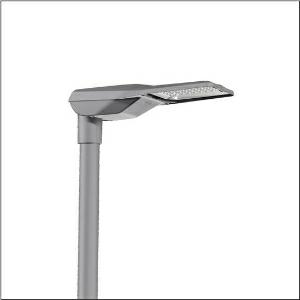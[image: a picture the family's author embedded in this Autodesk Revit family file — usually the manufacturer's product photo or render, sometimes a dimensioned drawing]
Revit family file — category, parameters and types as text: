
# Revit family: streetlight_sl_21_iq_mini___p0_8ab_5xe2r31d08jb_fb45
name_source: partatom
category: Lighting Fixtures
units: mm (PartAtom-declared; Revit-internal decimal feet)

## family parameters
Cut with Voids When Loaded = No
Host = Face
Light Source = No
Part Type = Normal
Room Calculation Point = No
Round Connector Dimension = Use Diameter
Shared = No

## types (1)
- --- (1 x LED, 9400 lm, 71.6 W, 3000K)
    Apparent Load = 72 VA
    CIE Flux Codes = 39 72 97 100 100
    Color Rendering = 70
    Color Temperature = 3000K
    Default Elevation = 1800 mm
    Description = Streetlight SL 21 iQ mini, mast luminaire, primary light control with lens, of PMMA, primary optical cover: cover, of toughened safety glass, transparent, light distribution: P0.8aB, light emission: direct distribution, primary light characteristic: asymmetric, installation type: post-top, side-entry, LED, High Power LED, rated luminous flux: 9.400lm, luminous efficacy: 131lm/W, light colour: 730, colour temperature: 3000K, control gear: iQ-Comfort, control: pre-setting: linear dimming characteristic, Auto-Match, Temp-Guard, Lumen-Switch, Night-Set, Smart-Wire, Light-Fading, Desk-Remote (wireless, voltage-free reading and setting of iQ features in the workshop via application-optimized NFC function/RFID function), optimised constant luminous flux control (CLO 2.0), mains connection: 220..240V, AC, 50/60Hz, start of lifetime: 72W, end of service life: 75W, reduction: 33W, luminaire housing, of diecast aluminium, powder-coated, SITECO metallic grey (DB 702S), corrosivity category C5 high according to DIN EN ISO 12944, please order mast flange separately, inclination adjustable: 0°, 5°, 10°, 15°, sealing non-destructively replaceable, multi-level sealing system, length: 628mm, width: 235mm, height: 110mm, mast flange for spigot size: 42mm (side-entry): 5XC10008XM4, 60/48mm (side-entry/post-top): 5XC10108XM2, 76/60mm (side-entry/post-top): 5XC10108XM1, mounting height: 4..8m, protection rating (complete): IP66, insulation class (complete): insulation class II (safety insulation), certification: CE, ENEC, ENEC+, VDE, impact resistance: IK10, permissible operating ambient temperature for outdoor applications: -40..+50°C, standard-compliant lighting for roads and squares, packaging unit: 1 piece

Light Distribution: P0.8aB
    Height = 110 mm
    Lamp = 1 x LED
    Lamp Light Flux = 9400 lm
    Lamp Power = 71.6 W
    Lamp count = 1
    Length = 625 mm
    Luminous efficacy = 131 lm/W
    Manufacturer = Siteco
    ModVariant = No
    Model = 5XE2R31D08JB
    Number of Poles = 1
    OnlyDefault = Yes
    Power Factor = 1
    Product Name = Streetlight SL 21 iQ mini | P0.8aB
    Product group = mast luminaire | pylon top
    ProductGroupID = 6100
    Protection Class = Protection class II
    Protection Degree = IP 66
    RLX_Detail_Level = 1
    RLX_Emergency_Light_Flux = 0 lm
    RLX_Emergency_Type = 0
    RLX_Emergency_Type_DB = No
    RlxData = <blob elided: 91921 chars, md5=eba938f1>
    Socket = socket
    Standby Power = 0 W
    System Light Flux = 9400 lm
    System Power = 72 W
    Type Comments = factory setting: luminous flux: 100 % | dim-lin: 254 | 746 mA
    Type Image = l_1003519.jpg
    URL = http://relux.com
    VarID = @adj_078877
    Voltage = 0 V
    Weight = 0.00 kg
    Width = 234 mm

## geometry (parser evidence)
native form markers: Blend x4, Sweep x10
no freeform markers — native parametric forms only
